# Revit family: G220760JX-008_JES1750ML
name_source: partatom
category: Specialty Equipment
units: mm (PartAtom-declared; Revit-internal decimal feet)

## family parameters
Always vertical = Yes
Cut with Voids When Loaded = No
Enable Cutting in Views = No
Maintain Annotation Orientation = No
Part Type = Normal
Room Calculation Point = No
Round Connector Dimension = Use Diameter
Shared = No
Work Plane-Based = No

## types (1)
- JES1750ML
    Amps = 0 A
    Back Pannle Mat = ARCAT - Metal - Aluminum
    Body Material = ARCAT - Metal - Steel - Stainless
    Clearance Material = ARCAT - Clearance
    Cooking Grate Material = ARCAT - Metal - Cast Iron 1/4" Plate
    Cooktop Material = ARCAT - Glass - Gray
    Default Elevation = 0 "
    Depth = 28.6 "
    Description = 30" RISE™ ELECTRIC DOWNDRAFT SLIDE-IN RANGE
Cuisinière électrique coulissante à évacuation descendante de 30 po
    Dimension Guide = http://whirlpool.com
    Display Panel Material = ARCAT - Glass - Black
    Door Material = ARCAT - Metal - Steel - Door
    Family Name = RISE Radiant Downdraft Slide In Range
    Feature 1 = True Convection
Convection véritable
    Feature 2 = Downdraft Ventilation
Évacuation descendante
    Feature 3 = Die-Cast Metal Knobs
Boutons en métal moulé sous pre
    Glass Material = ARCAT - Glass - Tempered - Black
    Handle Material = ARCAT - Metal - Steel -Gray - Light
    Height = 36 "
    Knob Material = ARCAT - Metal - Steel -Gray - Light
    Leg Material = ARCAT - Plastic - Black
    Voltage = 0 V
    Width = 29.9 "

## geometry (parser evidence)
native form markers: Sweep x6
no freeform markers — native parametric forms only
